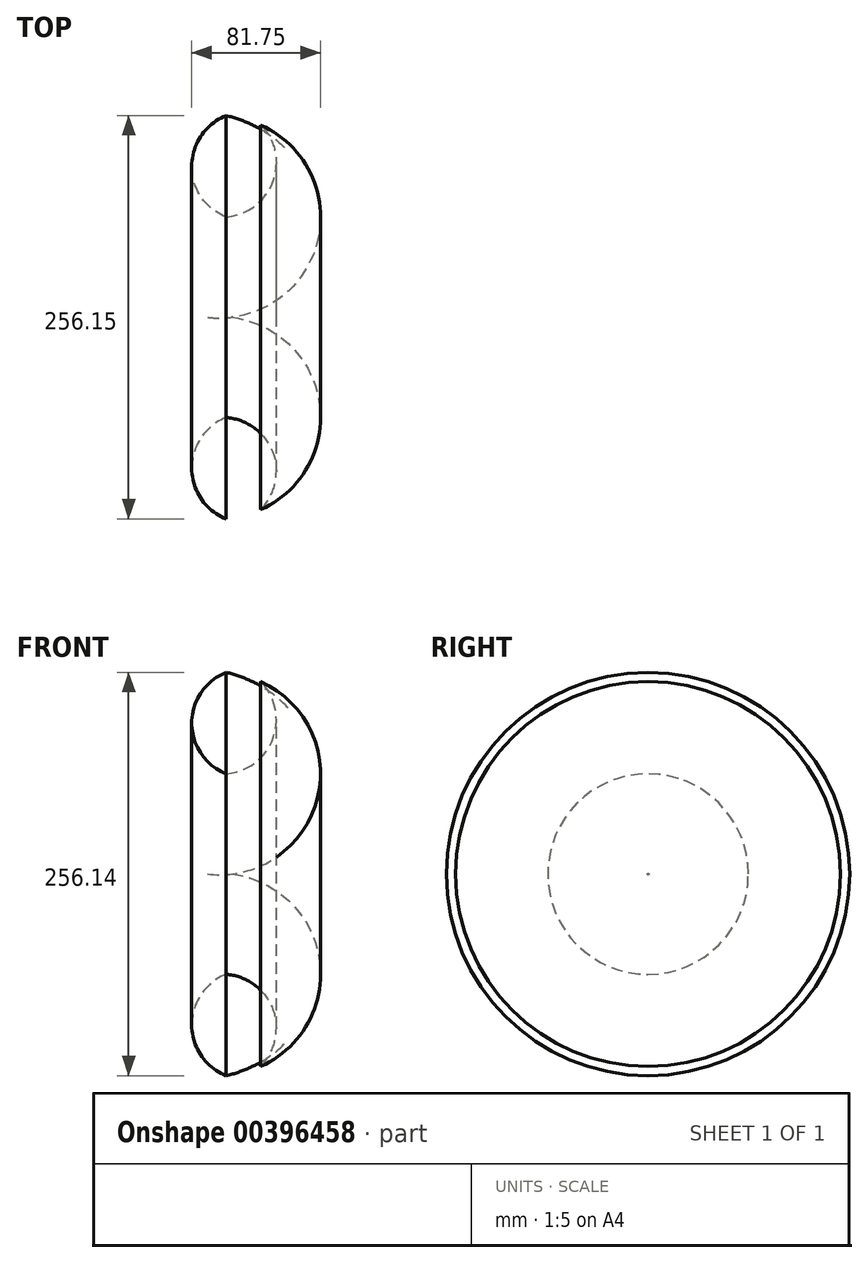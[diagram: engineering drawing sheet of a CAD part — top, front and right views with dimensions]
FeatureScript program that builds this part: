
annotation { "Feature Type Name" : "Feature", "Feature Type Description" : "" }
export const myFeature = defineFeature(function(context is Context, id is Id, definition is map)
    precondition{}
    {
        {
            var Q0;
            Q0=qCreatedBy(makeId("Top.planeOp"),FACE);
            var sketch = newSketch(context, id + "F0", { "sketchPlane" : qUnion([Q0])});
            skArc(sketch, "E0", {"start": v(-88.89, -85.58) * mm, "mid": v(-33.14, -31.55) * mm, "end": v(-70.32, 36.6) * mm});
            skArc(sketch, "E1", {"start": v(-92.28, -21.91) * mm, "mid": v(-62.65, 0.35) * mm, "end": v(-70.32, 36.6) * mm});
            skArc(sketch, "E2", {"start": v(-92.28, 42.5) * mm, "mid": v(-114.17, 10.3) * mm, "end": v(-92.28, -21.91) * mm});
            skArc(sketch, "E3", {"start": v(-92.28, 42.5) * mm, "mid": v(-176.3, 5.57) * mm, "end": v(-165.64, -85.58) * mm});
            skLineSegment(sketch, "E4", {"start": v(-165.64, -85.58) * mm, "end": v(-88.89, -85.58) * mm});
            skSolve(sketch);
        }
        {
            var Q0;
            Q0=makeQuery(id+"F0.imprint","IMPRINT",FACE,{"disambiguationData":[TD([[makeQuery(id+"F0.imprint","IMPRINT",EDGE,{"derivedFrom":sQuery(id+"F0.wireOp",EDGE,"E0")}),1.0]])]});
            var Q1;
            Q1=sQuery(id+"F0.wireOp",EDGE,"E4");
            revolve(context, id + "F1", {"entities" : qUnion([Q0]), "axis" : qUnion([Q1]), "revolveType" : RevolveType.FULL});
        }
    });
